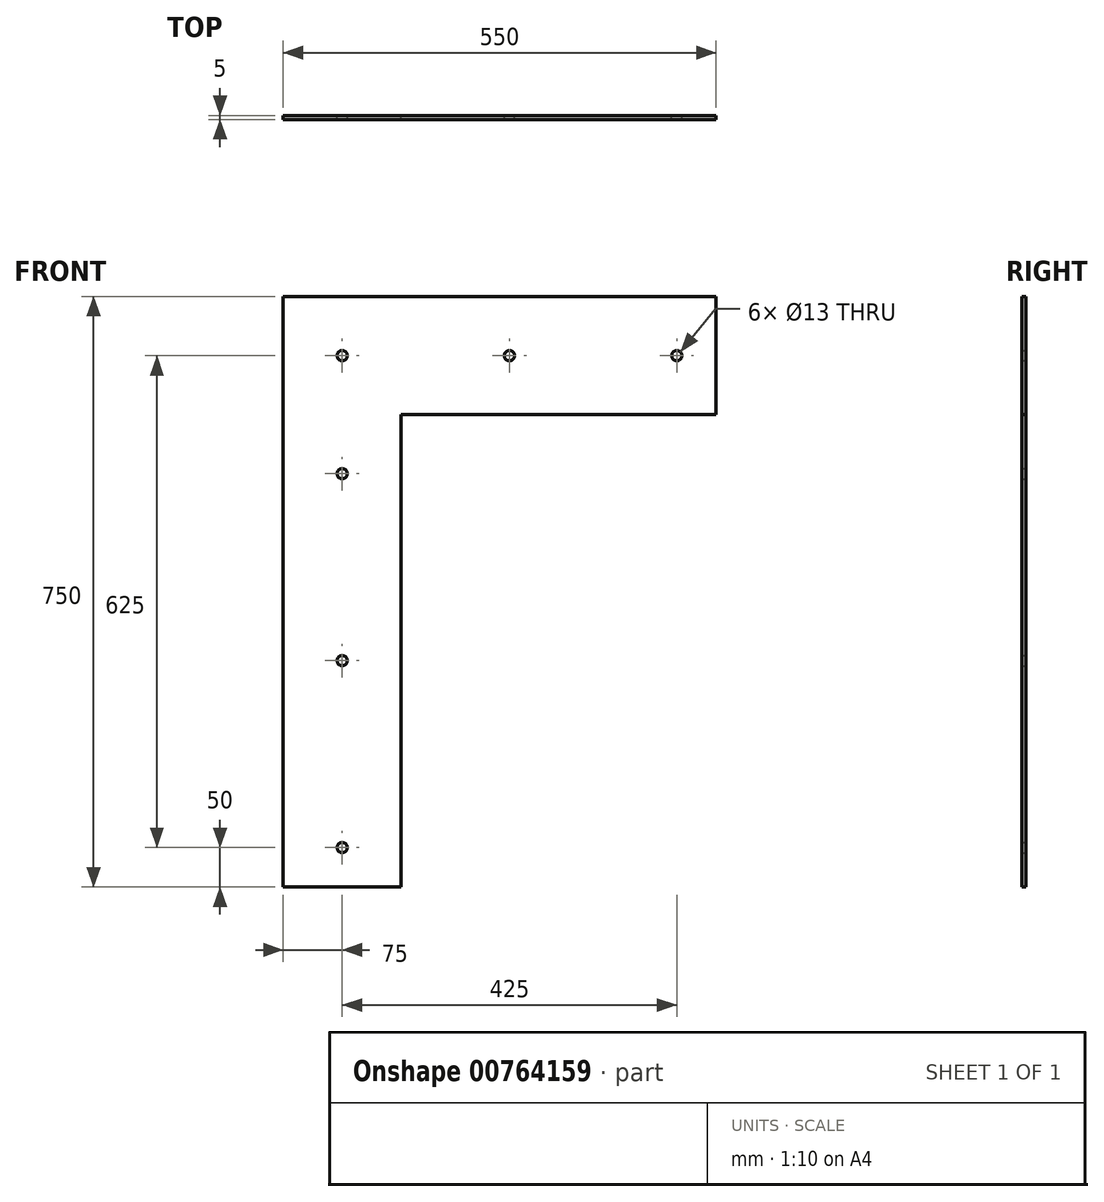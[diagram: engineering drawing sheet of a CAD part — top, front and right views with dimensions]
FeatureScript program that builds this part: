
annotation { "Feature Type Name" : "Feature", "Feature Type Description" : "" }
export const myFeature = defineFeature(function(context is Context, id is Id, definition is map)
    precondition{}
    {
        {
            var Q0;
            Q0=qCreatedBy(makeId("Front.planeOp"),FACE);
            var sketch = newSketch(context, id + "F0", { "sketchPlane" : qUnion([Q0])});
            skLineSegment(sketch, "E0", {"start": v(0, 0) * mm, "end": v(0, 750) * mm});
            skLineSegment(sketch, "E1", {"start": v(0, 750) * mm, "end": v(550, 750) * mm});
            skLineSegment(sketch, "E2", {"start": v(550, 750) * mm, "end": v(550, 600) * mm});
            skLineSegment(sketch, "E3", {"start": v(550, 600) * mm, "end": v(150, 600) * mm});
            skLineSegment(sketch, "E4", {"start": v(150, 600) * mm, "end": v(150, 0) * mm});
            skLineSegment(sketch, "E5", {"start": v(150, 0) * mm, "end": v(0, 0) * mm});
            skCircle(sketch, "E6", {"center": v(500, 675) * mm, "radius": 6.5 * mm});
            skCircle(sketch, "E7", {"center": v(287.5, 675) * mm, "radius": 6.5 * mm});
            skCircle(sketch, "E8", {"center": v(75, 675) * mm, "radius": 6.5 * mm});
            skCircle(sketch, "E9", {"center": v(75, 50) * mm, "radius": 6.5 * mm});
            skPoint(sketch, "E9.centerSnap0", {"position": v(75, 0) * mm});
            skCircle(sketch, "E10", {"center": v(75, 525) * mm, "radius": 6.5 * mm});
            skCircle(sketch, "E11", {"center": v(75, 287.5) * mm, "radius": 6.5 * mm});
            skSolve(sketch);
        }
        {
            var Q0;
            Q0=makeQuery(id+"F0.imprint","IMPRINT",FACE,{"disambiguationData":[TD([[makeQuery(id+"F0.imprint","IMPRINT",EDGE,{"derivedFrom":sQuery(id+"F0.wireOp",EDGE,"E0")}),-1.0]])]});
            extrude(context, id + "F1", {"entities" : qUnion([Q0]), "depth" : 5 * mm, "offsetDistance" : 25 * mm});
        }
    });
